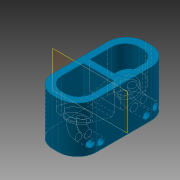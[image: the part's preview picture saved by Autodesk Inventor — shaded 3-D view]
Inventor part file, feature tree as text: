
AUTODESK INVENTOR PART (.ipt)
format: ipt  version: 2015 SP2 (Build 190223200, 223)  size: 238,080 bytes
history: native  units: in
note: dims shown in document units (in); Inventor stores cm internally (conversion verified against a paired STEP export)
features: extrude x4, mirror x4, sketch x4, plane x2, fillet x2, revolve x1
ambient origin geometry x8: Origin, YZ Plane, XZ Plane, XY Plane, X Axis, Y Axis, Z Axis, Center Point
bodies: Solid1 (feature_tree)
feature tree (17):
  extrude  "Extrusion1"  TaperAngle=105.0deg  [1 undecoded]
  extrude  "Extrusion2"  Depth=0.28in TaperAngle=0.0deg
  plane  "Work Plane1"
  mirror  "Mirror1"
  plane  "Work Plane2"
  extrude  "Extrusion3"  Depth=0.18in
  mirror  "Mirror2"
  fillet  "Fillet4"  Radius=0.265in
  fillet  "Fillet5"  Radius=0.04in
  revolve  "Revolution1"  Angle=90.0deg
  mirror  "Mirror3"
  extrude  "Extrusion6"  Depth=0.15in
  mirror  "Mirror10"
  sketch  "Sketch2"  dims[d0=0.425in d1=105.0deg]
  sketch  "Sketch3"  dims[d8=0.03in d10=0.28in d11=0.0in]
  sketch  "Sketch4"  dims[d12=0.06in d13=0.0in d14=0.18in d15=0.265in d16=0.04in d17=0.0in]
  sketch  "Sketch6"  dims[d18=0.045in d20=90.0deg d33=0.15in d34=0.425in d35=0.03in d36=0.07in d41=0.125in d42=0.175in d43=0.045in d44=0.065in d45=1.0in d46=0.0in]
note: 1 required parameter value undecoded (feature->parameter linkage not recoverable at this tier; creation-order binding heuristic only, values carry confidence <= 0.55)
